# Revit family: Plumbing_Fixture-Grohe-Tempesta-Shower-Rail-600mm-27523000-13-METRIC
name_source: partatom
category: Furniture
revit_build: Autodesk Revit 2013 (Build: 20121003_2115(x64)
units: mm (PartAtom-declared; Revit-internal decimal feet)

## types (1)
- Rainshower Shower Rail 27523000
    ADA Compliant = Yes
    Assembly Code = C1030220
    AssetType = Fixed
    Barcode = 0
    Bracket Width = 30 mm  [stored 0.0984252 ft]
    ClassificationName = Uniclass 1.4
    ClassificationValue = L725111
    Cost = 0 $
    Default Elevation = 600 mm
    Description = Shower rail, 600mm with wall holders made of metal, glide element and swivel holder, adjustable distance between wall shower holders for adaption to existing drillings.
    DocumentationCertificates = http://www.grohe.co.uk
    DocumentationInstallationGuide = http://www.grohe.co.uk
    DocumentationLiterature = http://www.grohe.co.uk
    DocumentationTechnical = http://www.grohe.co.uk
    DurationUnit = Years
    Ecojoy = No
    ExpectedLife = 0
    Faucet Material = Grohe-Chrome
    Keynote = N13
    Length = 620 mm  [stored 2.03412 ft]
    Low Emitting Material = Yes
    MaintenanceInformation = http://cdn08.grohe.com
    Manufacturer = Grohe AG
    Model = Rainshower shower rail 600
    Name = Rainshower shower rail 600
    Percentage of Recycled Content = 0
    Product Page URL = http://www.grohe.co.uk
    SerialNumber = 0
    Spare Parts List = http://www.grohe.co.uk
    TagNumber = 0
    Type Comments = Shower Rail, 600mm, adjustable distance between wall shower holders for adaption to existing drillings
    TypeName = Rainshower shower rail 600
    URL = www.grohe.com
    Uniclass2 = Pr_40_30_96
    WarrantyDurationUnit = Years
    _BIMspec_GUID = 0
    _current revision = 1
    _distributed by = www.bimstore.co.uk

note: [stored X ft] marks values corroborated as IEEE doubles in the binary element streams (Revit-internal decimal feet)

## geometry (parser evidence)
native form markers: Blend x4, Sweep x5
no freeform markers — native parametric forms only
